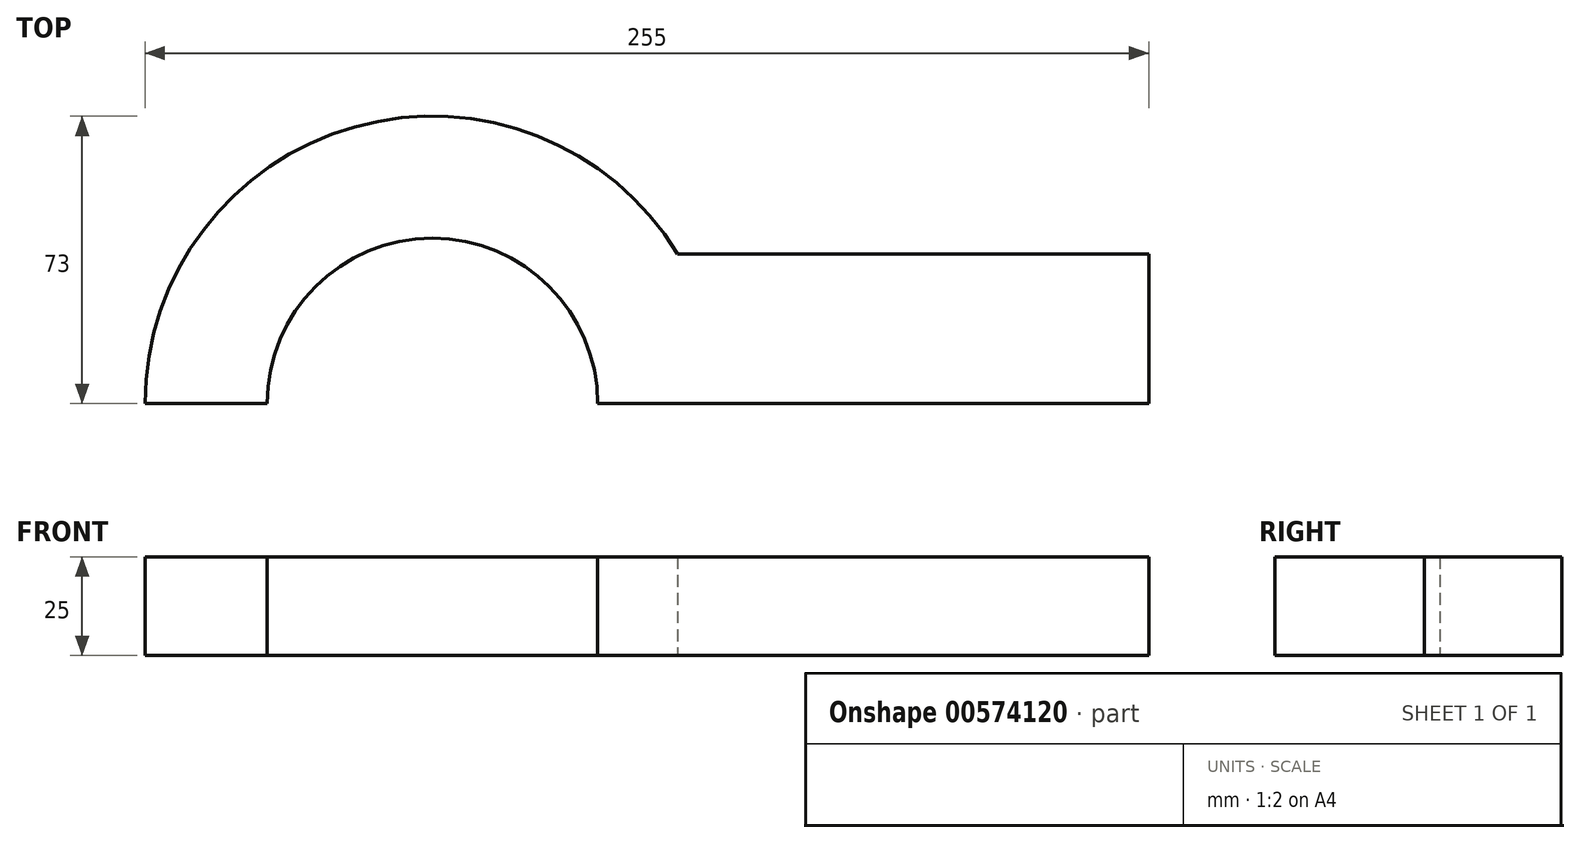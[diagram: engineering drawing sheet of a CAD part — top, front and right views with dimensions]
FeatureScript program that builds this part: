
annotation { "Feature Type Name" : "Feature", "Feature Type Description" : "" }
export const myFeature = defineFeature(function(context is Context, id is Id, definition is map)
    precondition{}
    {
        {
            var Q0;
            Q0=qCreatedBy(makeId("Top.planeOp"),FACE);
            var sketch = newSketch(context, id + "F0", { "sketchPlane" : qUnion([Q0])});
            skArc(sketch, "E0", {"start": v(42, 0) * mm, "mid": v(0, 42) * mm, "end": v(-42, 0) * mm});
            skArc(sketch, "E1", {"start": v(62.33, 38) * mm, "mid": v(-19.73, 70.28) * mm, "end": v(-73, 0) * mm});
            skLineSegment(sketch, "E2", {"start": v(-73, 0) * mm, "end": v(-42, 0) * mm});
            skLineSegment(sketch, "E3", {"start": v(42, 0) * mm, "end": v(73, 0) * mm});
            skLineSegment(sketch, "E4.bottom", {"start": v(62.33, 0) * mm, "end": v(182, 0) * mm});
            skLineSegment(sketch, "E4.top", {"start": v(62.33, 38) * mm, "end": v(182, 38) * mm});
            skLineSegment(sketch, "E4.left", {"start": v(62.33, 0) * mm, "end": v(62.33, 38) * mm, "construction": true});
            skLineSegment(sketch, "E4.right", {"start": v(182, 0) * mm, "end": v(182, 38) * mm});
            skSolve(sketch);
        }
        {
            var Q0;
            Q0 = qSketchRegion(id + "F0", true);
            extrude(context, id + "F1", {"entities" : qUnion([Q0]), "depth" : 25 * mm, "offsetDistance" : 25 * mm});
        }
    });
